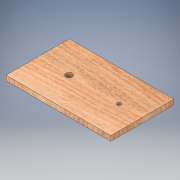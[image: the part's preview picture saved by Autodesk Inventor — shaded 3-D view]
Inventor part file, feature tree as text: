
AUTODESK INVENTOR PART (.ipt)
format: ipt  version: 2017 (Build 210142000, 142)  size: 128,512 bytes
history: native  units: in
note: dims shown in document units (in); Inventor stores cm internally (conversion verified against a paired STEP export)
features: extrude x2, sketch x2
ambient origin geometry x8: Origin, YZ Plane, XZ Plane, XY Plane, X Axis, Y Axis, Z Axis, Center Point
bodies: Solid1 (feature_tree)
feature tree (4):
  extrude  "Extrusion1"  Depth=0.4688in TaperAngle=0.0deg
  extrude  "Extrusion2"  Depth=0.4688in
  sketch  "Sketch1"  dims[d0=6.0in d1=9.9688in d2=2.2188in d3=0.375in d4=0.4688in d5=0.0in]
  sketch  "Sketch2"  dims[d6=6.9688in d7=0.625in d8=0.4688in d9=0.0in]
